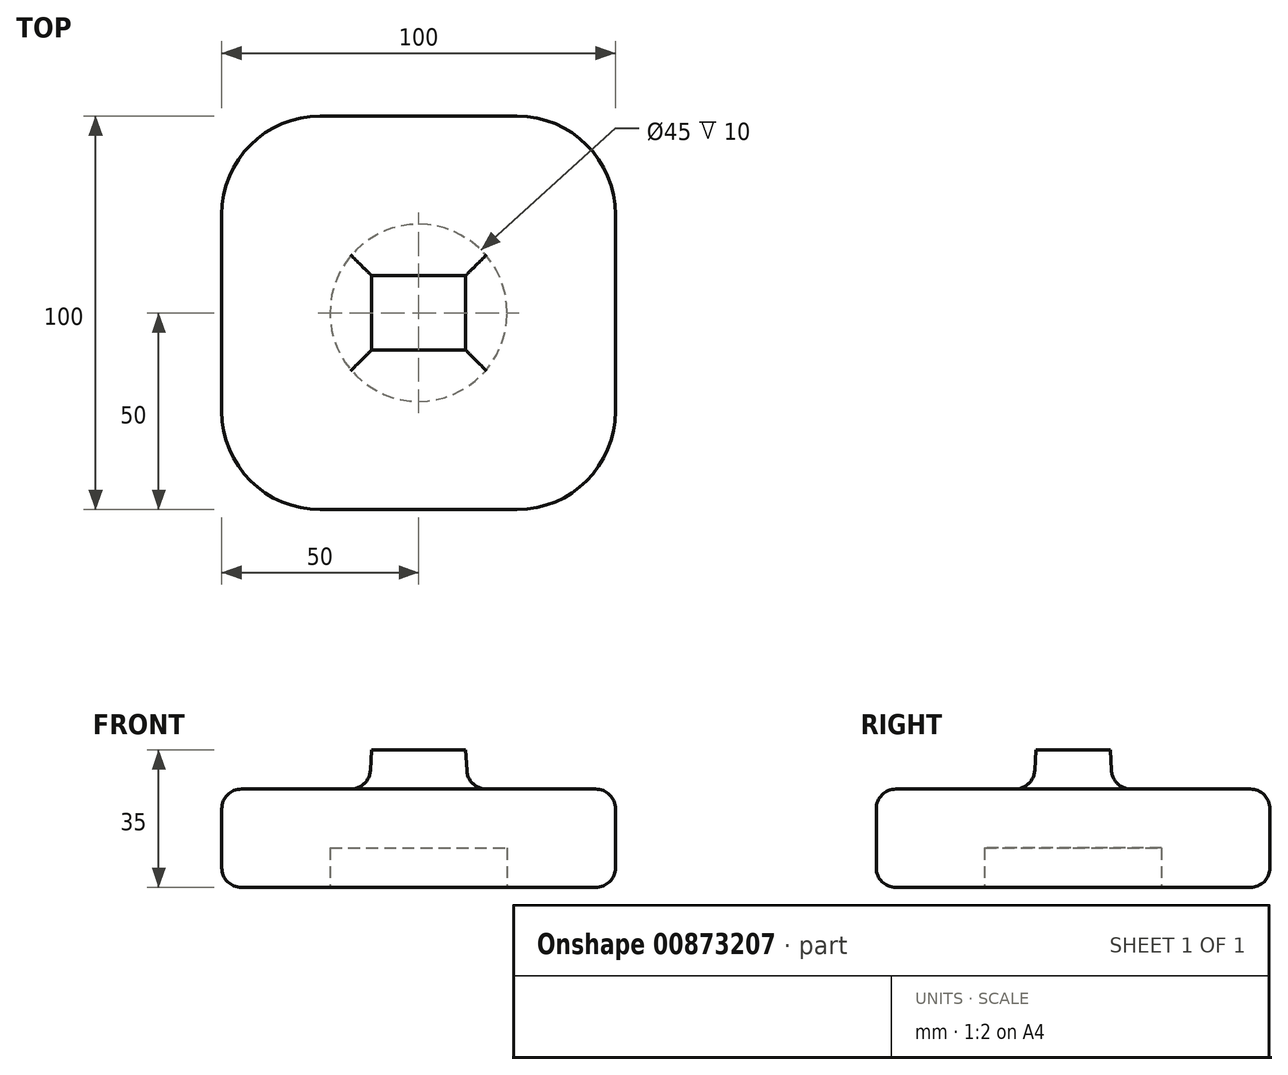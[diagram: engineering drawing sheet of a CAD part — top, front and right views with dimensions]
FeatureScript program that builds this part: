
annotation { "Feature Type Name" : "Feature", "Feature Type Description" : "" }
export const myFeature = defineFeature(function(context is Context, id is Id, definition is map)
    precondition{}
    {
        {
            assignVariable(context, id + "F0", {"name" : "thickness", "anyValue" : 25});
        }
        {
            var Q0;
            Q0=qCreatedBy(makeId("Top.planeOp"),FACE);
            var sketch = newSketch(context, id + "F1", { "sketchPlane" : qUnion([Q0])});
            skLineSegment(sketch, "E0.bottom", {"start": v(50, -50) * mm, "end": v(-50, -50) * mm});
            skLineSegment(sketch, "E0.top", {"start": v(50, 50) * mm, "end": v(-50, 50) * mm});
            skLineSegment(sketch, "E0.left", {"start": v(50, -50) * mm, "end": v(50, 50) * mm});
            skLineSegment(sketch, "E0.right", {"start": v(-50, -50) * mm, "end": v(-50, 50) * mm});
            skPoint(sketch, "E0.middle", {"position": v(0, 0) * mm});
            skSolve(sketch);
        }
        {
            var Q0;
            Q0 = qSketchRegion(id + "F1", true);
            extrude(context, id + "F2", {"entities" : qUnion([Q0]), "depth" : getVariable(context, 'thickness') * mm, "offsetDistance" : 25 * mm});
        }
        {
            var Q0;
            Q0=makeQuery(id+"F2.opExtrude","SWEPT_EDGE",EDGE,{"disambiguationData":[OSD([sQuery(id+"F1.wireOp",EDGE,"E0.bottom"),sQuery(id+"F1.wireOp",EDGE,"E0.left")])]});
            var Q1;
            Q1=makeQuery(id+"F2.opExtrude","SWEPT_EDGE",EDGE,{"disambiguationData":[OSD([sQuery(id+"F1.wireOp",EDGE,"E0.bottom"),sQuery(id+"F1.wireOp",EDGE,"E0.right")])]});
            var Q2;
            Q2=makeQuery(id+"F2.opExtrude","SWEPT_EDGE",EDGE,{"disambiguationData":[OSD([sQuery(id+"F1.wireOp",EDGE,"E0.top"),sQuery(id+"F1.wireOp",EDGE,"E0.right")])]});
            var Q3;
            Q3=makeQuery(id+"F2.opExtrude","SWEPT_EDGE",EDGE,{"disambiguationData":[OSD([sQuery(id+"F1.wireOp",EDGE,"E0.top"),sQuery(id+"F1.wireOp",EDGE,"E0.left")])]});
            fillet(context, id + "F3", {"entities" : qUnion([Q0, Q1, Q2, Q3]), "radius" : 25 * mm, "tangentPropagation" : true, "allowEdgeOverflow" : false});
        }
        {
            var Q0;
            Q0=makeQuery(id+"F2.opExtrude","CAP_FACE",FACE,{"disambiguationData":[OSD([sQuery(id+"F1.wireOp",EDGE,"E0.bottom"),sQuery(id+"F1.wireOp",EDGE,"E0.top"),sQuery(id+"F1.wireOp",EDGE,"E0.left"),sQuery(id+"F1.wireOp",EDGE,"E0.right")])],"isStart":false});
            var Q1;
            Q1=makeQuery(id+"F2.opExtrude","CAP_FACE",FACE,{"disambiguationData":[OSD([sQuery(id+"F1.wireOp",EDGE,"E0.bottom"),sQuery(id+"F1.wireOp",EDGE,"E0.top"),sQuery(id+"F1.wireOp",EDGE,"E0.left"),sQuery(id+"F1.wireOp",EDGE,"E0.right")])],"isStart":true});
            fillet(context, id + "F4", {"entities" : qUnion([Q0, Q1]), "radius" : 5 * mm, "tangentPropagation" : true, "allowEdgeOverflow" : false});
        }
        {
            var Q0;
            Q0=makeQuery(id+"F2.opExtrude","CAP_FACE",FACE,{"disambiguationData":[OSD([sQuery(id+"F1.wireOp",EDGE,"E0.bottom"),sQuery(id+"F1.wireOp",EDGE,"E0.top"),sQuery(id+"F1.wireOp",EDGE,"E0.left"),sQuery(id+"F1.wireOp",EDGE,"E0.right")])],"isStart":false});
            var sketch = newSketch(context, id + "F5", { "sketchPlane" : qUnion([Q0])});
            skLineSegment(sketch, "E1.bottom", {"start": v(12.5, 10) * mm, "end": v(-12.5, 10) * mm});
            skLineSegment(sketch, "E1.top", {"start": v(12.5, -10) * mm, "end": v(-12.5, -10) * mm});
            skLineSegment(sketch, "E1.left", {"start": v(12.5, 10) * mm, "end": v(12.5, -10) * mm});
            skLineSegment(sketch, "E1.right", {"start": v(-12.5, 10) * mm, "end": v(-12.5, -10) * mm});
            skPoint(sketch, "E1.middle", {"position": v(0, 0) * mm});
            skLineSegment(sketch, "E2", {"start": v(0, 10) * mm, "end": v(0, 45) * mm, "construction": true});
            skLineSegment(sketch, "E3", {"start": v(0, -10) * mm, "end": v(0, -45) * mm, "construction": true});
            skSolve(sketch);
        }
        {
            var Q0;
            Q0 = qSketchRegion(id + "F5", true);
            extrude(context, id + "F6", {"entities" : qUnion([Q0]), "operationType" : NewBodyOperationType.ADD, "depth" : 10 * mm, "offsetDistance" : 25 * mm, "hasDraft" : true, "draftAngle" : 3 * degree, "draftPullDirection" : true});
        }
        {
            var Q0;
            Q0=makeQuery(id+"F2.opExtrude","CAP_FACE",FACE,{"disambiguationData":[OSD([sQuery(id+"F1.wireOp",EDGE,"E0.bottom"),sQuery(id+"F1.wireOp",EDGE,"E0.top"),sQuery(id+"F1.wireOp",EDGE,"E0.left"),sQuery(id+"F1.wireOp",EDGE,"E0.right")])],"isStart":false});
            fillet(context, id + "F7", {"entities" : qUnion([Q0]), "radius" : 5 * mm, "tangentPropagation" : true, "allowEdgeOverflow" : false});
        }
        {
            var Q0;
            Q0=makeQuery(id+"F2.opExtrude","CAP_FACE",FACE,{"disambiguationData":[OSD([sQuery(id+"F1.wireOp",EDGE,"E0.bottom"),sQuery(id+"F1.wireOp",EDGE,"E0.top"),sQuery(id+"F1.wireOp",EDGE,"E0.left"),sQuery(id+"F1.wireOp",EDGE,"E0.right")])],"isStart":true});
            var sketch = newSketch(context, id + "F8", { "sketchPlane" : qUnion([Q0])});
            skCircle(sketch, "E4", {"center": v(0, 0) * mm, "radius": 22.5 * mm});
            skLineSegment(sketch, "E5", {"start": v(-50, -50) * mm, "end": v(50, 50) * mm, "construction": true});
            skSolve(sketch);
        }
        {
            var Q0;
            Q0 = qSketchRegion(id + "F8", true);
            extrude(context, id + "F9", {"entities" : qUnion([Q0]), "operationType" : NewBodyOperationType.REMOVE, "oppositeDirection" : true, "depth" : 10 * mm, "offsetDistance" : 25 * mm});
        }
    });
